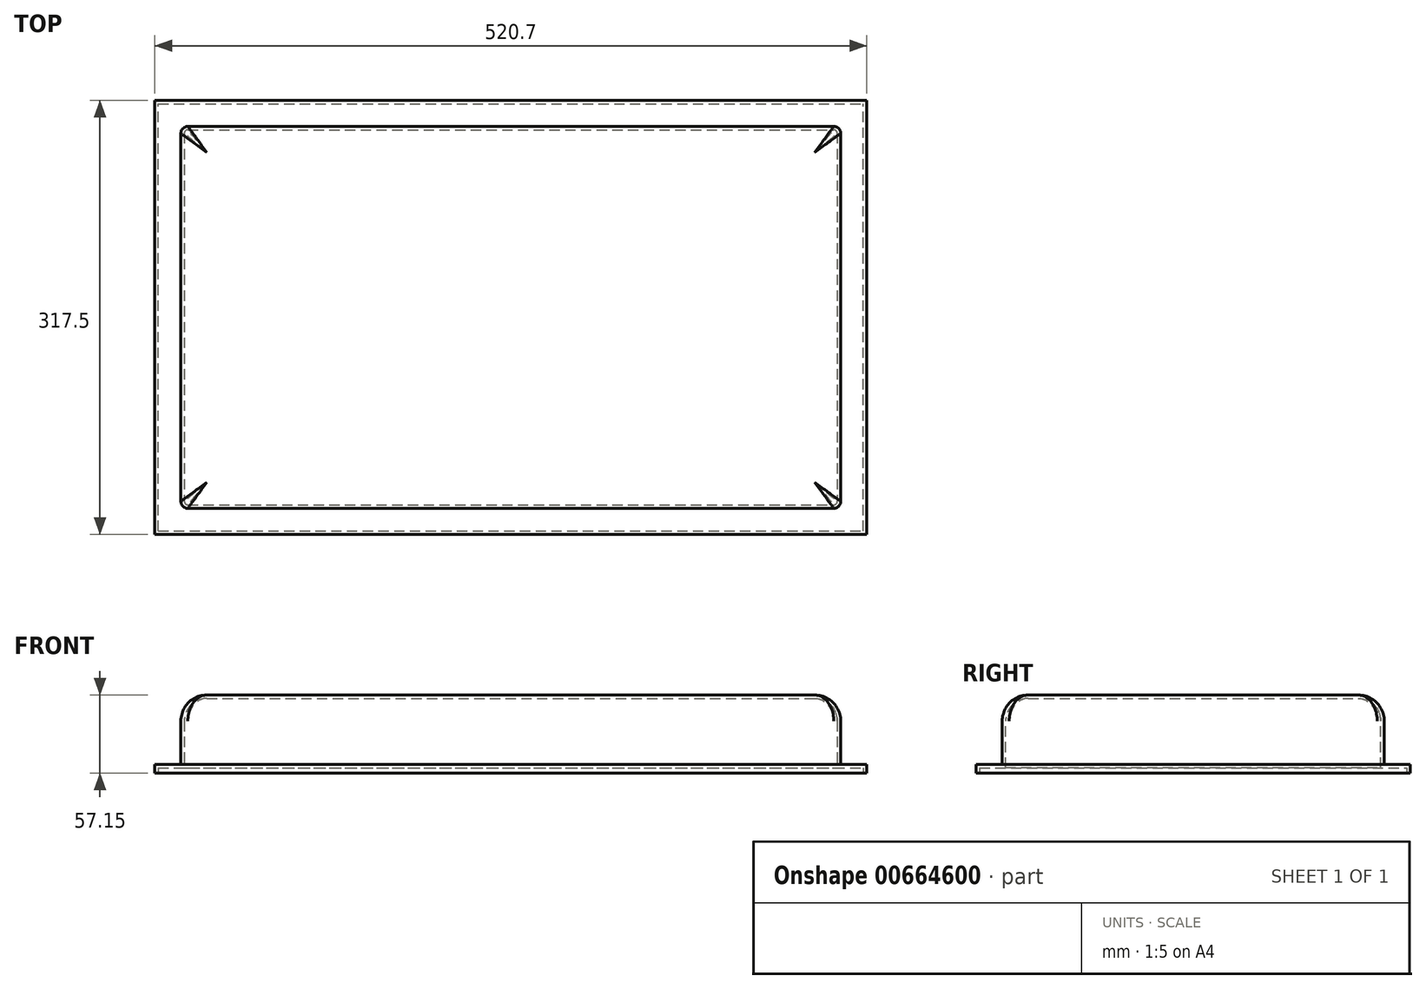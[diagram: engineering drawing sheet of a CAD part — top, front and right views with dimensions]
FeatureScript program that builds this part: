
annotation { "Feature Type Name" : "Feature", "Feature Type Description" : "" }
export const myFeature = defineFeature(function(context is Context, id is Id, definition is map)
    precondition{}
    {
        {
            var Q0;
            Q0=qCreatedBy(makeId("Top.planeOp"),FACE);
            var sketch = newSketch(context, id + "F0", { "sketchPlane" : qUnion([Q0])});
            skLineSegment(sketch, "E0.bottom", {"start": v(0, 0) * mm, "end": v(520.7, 0) * mm});
            skLineSegment(sketch, "E0.top", {"start": v(0, 317.5) * mm, "end": v(520.7, 317.5) * mm});
            skLineSegment(sketch, "E0.left", {"start": v(0, 0) * mm, "end": v(0, 317.5) * mm});
            skLineSegment(sketch, "E0.right", {"start": v(520.7, 0) * mm, "end": v(520.7, 317.5) * mm});
            skSolve(sketch);
        }
        {
            var Q0;
            Q0=makeQuery(id+"F0.imprint","IMPRINT",FACE,{"disambiguationData":[TD([[makeQuery(id+"F0.imprint","IMPRINT",EDGE,{"derivedFrom":sQuery(id+"F0.wireOp",EDGE,"E0.bottom")}),1.0]])]});
            extrude(context, id + "F1", {"entities" : qUnion([Q0]), "depth" : 6.35 * mm, "offsetDistance" : 25.4 * mm});
        }
        {
            var Q0;
            Q0=makeQuery(id+"F1.opExtrude","CAP_FACE",FACE,{"disambiguationData":[OSD([sQuery(id+"F0.wireOp",EDGE,"E0.bottom"),sQuery(id+"F0.wireOp",EDGE,"E0.top"),sQuery(id+"F0.wireOp",EDGE,"E0.left"),sQuery(id+"F0.wireOp",EDGE,"E0.right")])],"isStart":false});
            var sketch = newSketch(context, id + "F2", { "sketchPlane" : qUnion([Q0])});
            skLineSegment(sketch, "E1.bottom", {"start": v(19.05, 298.45) * mm, "end": v(501.65, 298.45) * mm});
            skLineSegment(sketch, "E1.top", {"start": v(19.05, 19.05) * mm, "end": v(501.65, 19.05) * mm});
            skLineSegment(sketch, "E1.left", {"start": v(19.05, 298.45) * mm, "end": v(19.05, 19.05) * mm});
            skLineSegment(sketch, "E1.right", {"start": v(501.65, 298.45) * mm, "end": v(501.65, 19.05) * mm});
            skSolve(sketch);
        }
        {
            var Q0;
            Q0=makeQuery(id+"F2.imprint","IMPRINT",FACE,{"disambiguationData":[TD([[makeQuery(id+"F2.imprint","IMPRINT",EDGE,{"derivedFrom":sQuery(id+"F2.wireOp",EDGE,"E1.bottom")}),-1.0]])]});
            extrude(context, id + "F3", {"entities" : qUnion([Q0]), "operationType" : NewBodyOperationType.ADD, "depth" : 50.8 * mm, "offsetDistance" : 25.4 * mm});
        }
        {
            var Q0;
            Q0=makeQuery(id+"F3.opExtrude","CAP_EDGE",EDGE,{"disambiguationData":[OSD([sQuery(id+"F2.wireOp",EDGE,"E1.left")])],"isStart":false});
            var Q1;
            Q1=makeQuery(id+"F3.opExtrude","CAP_EDGE",EDGE,{"disambiguationData":[OSD([sQuery(id+"F2.wireOp",EDGE,"E1.top")])],"isStart":false});
            var Q2;
            Q2=makeQuery(id+"F3.opExtrude","CAP_EDGE",EDGE,{"disambiguationData":[OSD([sQuery(id+"F2.wireOp",EDGE,"E1.right")])],"isStart":false});
            var Q3;
            Q3=makeQuery(id+"F3.opExtrude","CAP_EDGE",EDGE,{"disambiguationData":[OSD([sQuery(id+"F2.wireOp",EDGE,"E1.bottom")])],"isStart":false});
            fillet(context, id + "F4", {"entities" : qUnion([Q0, Q1, Q2, Q3]), "radius" : 19.05 * mm, "allowEdgeOverflow" : false});
        }
        {
            var Q0;
            Q0=makeQuery(id+"F3.opExtrude","SWEPT_EDGE",EDGE,{"disambiguationData":[OSD([sQuery(id+"F2.wireOp",EDGE,"E1.bottom"),sQuery(id+"F2.wireOp",EDGE,"E1.left")])]});
            var Q1;
            Q1=makeQuery(id+"F3.opExtrude","SWEPT_EDGE",EDGE,{"disambiguationData":[OSD([sQuery(id+"F2.wireOp",EDGE,"E1.top"),sQuery(id+"F2.wireOp",EDGE,"E1.left")])]});
            var Q2;
            Q2=makeQuery(id+"F3.opExtrude","SWEPT_EDGE",EDGE,{"disambiguationData":[OSD([sQuery(id+"F2.wireOp",EDGE,"E1.top"),sQuery(id+"F2.wireOp",EDGE,"E1.right")])]});
            var Q3;
            Q3=makeQuery(id+"F3.opExtrude","SWEPT_EDGE",EDGE,{"disambiguationData":[OSD([sQuery(id+"F2.wireOp",EDGE,"E1.bottom"),sQuery(id+"F2.wireOp",EDGE,"E1.right")])]});
            fillet(context, id + "F5", {"entities" : qUnion([Q0, Q1, Q2, Q3]), "radius" : 5.08 * mm, "tangentPropagation" : true, "allowEdgeOverflow" : false});
        }
        {
            var Q0;
            Q0=makeQuery(id+"F1.opExtrude","CAP_FACE",FACE,{"disambiguationData":[OSD([sQuery(id+"F0.wireOp",EDGE,"E0.bottom"),sQuery(id+"F0.wireOp",EDGE,"E0.top"),sQuery(id+"F0.wireOp",EDGE,"E0.left"),sQuery(id+"F0.wireOp",EDGE,"E0.right")])],"isStart":true});
            shell(context, id + "F6", {"entities" : qUnion([Q0]), "thickness" : 2.54 * mm});
        }
    });
